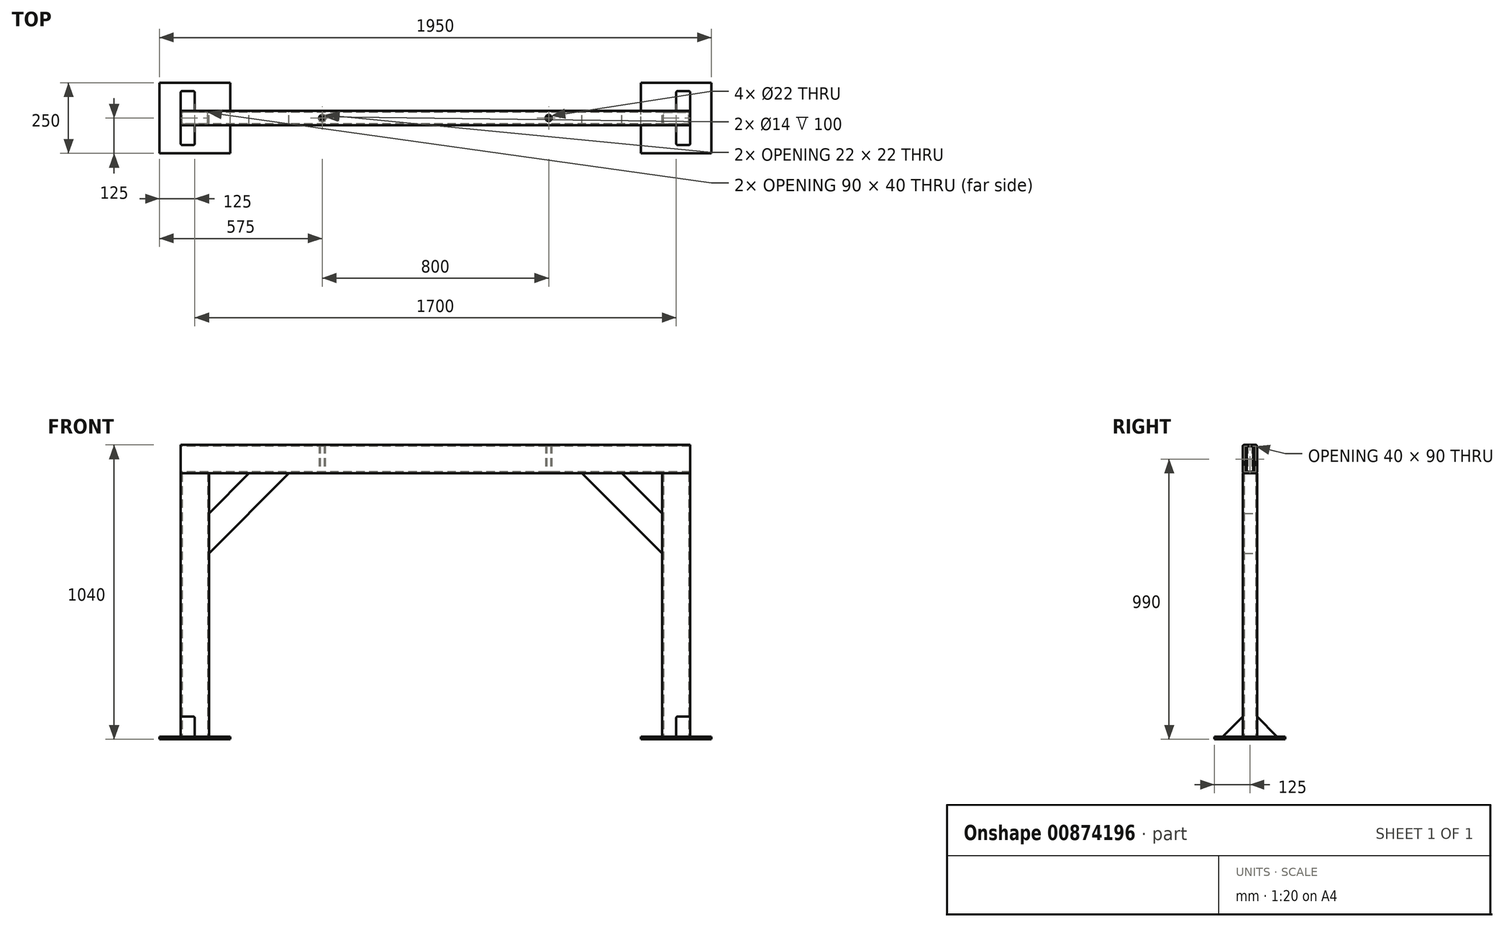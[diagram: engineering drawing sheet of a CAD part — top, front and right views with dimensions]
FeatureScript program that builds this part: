
annotation { "Feature Type Name" : "Feature", "Feature Type Description" : "" }
export const myFeature = defineFeature(function(context is Context, id is Id, definition is map)
    precondition{}
    {
        {
            var Q0;
            Q0=qCreatedBy(makeId("Top.planeOp"),FACE);
            var sketch = newSketch(context, id + "F0", { "sketchPlane" : qUnion([Q0])});
            skLineSegment(sketch, "E0.bottom", {"start": v(-804, -25) * mm, "end": v(-896, -25) * mm});
            skLineSegment(sketch, "E0.top", {"start": v(-804, 25) * mm, "end": v(-896, 25) * mm});
            skLineSegment(sketch, "E0.left", {"start": v(-800, -21) * mm, "end": v(-800, 21) * mm});
            skLineSegment(sketch, "E0.right", {"start": v(-900, -21) * mm, "end": v(-900, 21) * mm});
            skPoint(sketch, "E0.middle", {"position": v(-850, 0) * mm});
            skLineSegment(sketch, "E1.bottom", {"start": v(-808, -20) * mm, "end": v(-892, -20) * mm});
            skLineSegment(sketch, "E1.top", {"start": v(-808, 20) * mm, "end": v(-892, 20) * mm});
            skLineSegment(sketch, "E1.left", {"start": v(-805, -17) * mm, "end": v(-805, 17) * mm});
            skLineSegment(sketch, "E1.right", {"start": v(-895, -17) * mm, "end": v(-895, 17) * mm});
            skPoint(sketch, "E2.visualSharp", {"position": v(-895, 20) * mm});
            skArc(sketch, "E2.filletArc", {"start": v(-892, 20) * mm, "mid": v(-894.12, 19.12) * mm, "end": v(-895, 17) * mm});
            skPoint(sketch, "E3.visualSharp", {"position": v(-805, 20) * mm});
            skArc(sketch, "E3.filletArc", {"start": v(-805, 17) * mm, "mid": v(-805.88, 19.12) * mm, "end": v(-808, 20) * mm});
            skPoint(sketch, "E4.visualSharp", {"position": v(-805, -20) * mm});
            skArc(sketch, "E4.filletArc", {"start": v(-808, -20) * mm, "mid": v(-805.88, -19.12) * mm, "end": v(-805, -17) * mm});
            skPoint(sketch, "E5.visualSharp", {"position": v(-895, -20) * mm});
            skArc(sketch, "E5.filletArc", {"start": v(-895, -17) * mm, "mid": v(-894.12, -19.12) * mm, "end": v(-892, -20) * mm});
            skPoint(sketch, "E6.visualSharp", {"position": v(-900, 25) * mm});
            skArc(sketch, "E6.filletArc", {"start": v(-896, 25) * mm, "mid": v(-898.83, 23.83) * mm, "end": v(-900, 21) * mm});
            skPoint(sketch, "E7.visualSharp", {"position": v(-800, 25) * mm});
            skArc(sketch, "E7.filletArc", {"start": v(-800, 21) * mm, "mid": v(-801.17, 23.83) * mm, "end": v(-804, 25) * mm});
            skPoint(sketch, "E8.visualSharp", {"position": v(-800, -25) * mm});
            skArc(sketch, "E8.filletArc", {"start": v(-804, -25) * mm, "mid": v(-801.17, -23.83) * mm, "end": v(-800, -21) * mm});
            skPoint(sketch, "E9.visualSharp", {"position": v(-900, -25) * mm});
            skArc(sketch, "E9.filletArc", {"start": v(-900, -21) * mm, "mid": v(-898.83, -23.83) * mm, "end": v(-896, -25) * mm});
            skArc(sketch, "E10.MirrorCS", {"start": v(808, -20) * mm, "mid": v(805.88, -19.12) * mm, "end": v(805, -17) * mm});
            skArc(sketch, "E11.MirrorCS", {"start": v(800, 21) * mm, "mid": v(801.17, 23.83) * mm, "end": v(804, 25) * mm});
            skArc(sketch, "E12.MirrorCS", {"start": v(804, -25) * mm, "mid": v(801.17, -23.83) * mm, "end": v(800, -21) * mm});
            skArc(sketch, "E13.MirrorCS", {"start": v(892, 20) * mm, "mid": v(894.12, 19.12) * mm, "end": v(895, 17) * mm});
            skArc(sketch, "E14.MirrorCS", {"start": v(896, 25) * mm, "mid": v(898.83, 23.83) * mm, "end": v(900, 21) * mm});
            skArc(sketch, "E15.MirrorCS", {"start": v(805, 17) * mm, "mid": v(805.88, 19.12) * mm, "end": v(808, 20) * mm});
            skArc(sketch, "E16.MirrorCS", {"start": v(895, -17) * mm, "mid": v(894.12, -19.12) * mm, "end": v(892, -20) * mm});
            skArc(sketch, "E17.MirrorCS", {"start": v(900, -21) * mm, "mid": v(898.83, -23.83) * mm, "end": v(896, -25) * mm});
            skLineSegment(sketch, "E18.MirrorCS", {"start": v(900, -21) * mm, "end": v(900, 21) * mm});
            skPoint(sketch, "E19.MirrorP", {"position": v(850, 0) * mm});
            skLineSegment(sketch, "E20.MirrorCS", {"start": v(804, -25) * mm, "end": v(896, -25) * mm});
            skPoint(sketch, "E21.MirrorP", {"position": v(805, 20) * mm});
            skLineSegment(sketch, "E22.MirrorCS", {"start": v(805, -17) * mm, "end": v(805, 17) * mm});
            skLineSegment(sketch, "E23.MirrorCS", {"start": v(895, -17) * mm, "end": v(895, 17) * mm});
            skLineSegment(sketch, "E24.MirrorCS", {"start": v(800, -21) * mm, "end": v(800, 21) * mm});
            skLineSegment(sketch, "E25.MirrorCS", {"start": v(808, -20) * mm, "end": v(892, -20) * mm});
            skPoint(sketch, "E26.MirrorP", {"position": v(895, 20) * mm});
            skPoint(sketch, "E27.MirrorP", {"position": v(900, 25) * mm});
            skPoint(sketch, "E28.MirrorP", {"position": v(800, 25) * mm});
            skPoint(sketch, "E29.MirrorP", {"position": v(900, -25) * mm});
            skPoint(sketch, "E30.MirrorP", {"position": v(805, -20) * mm});
            skLineSegment(sketch, "E31.MirrorCS", {"start": v(808, 20) * mm, "end": v(892, 20) * mm});
            skLineSegment(sketch, "E32.MirrorCS", {"start": v(804, 25) * mm, "end": v(896, 25) * mm});
            skPoint(sketch, "E33.MirrorP", {"position": v(895, -20) * mm});
            skPoint(sketch, "E34.MirrorP", {"position": v(800, -25) * mm});
            skSolve(sketch);
        }
        {
            var Q0;
            Q0 = qSketchRegion(id + "F0", true);
            extrude(context, id + "F1", {"entities" : qUnion([Q0]), "depth" : 930 * mm, "offsetDistance" : 25 * mm});
        }
        {
            var Q0;
            Q0=makeQuery(id+"F1.opExtrude","SWEPT_FACE",FACE,{"disambiguationData":[OSD([sQuery(id+"F0.wireOp",EDGE,"E0.right")])]});
            var sketch = newSketch(context, id + "F2", { "sketchPlane" : qUnion([Q0])});
            skLineSegment(sketch, "E35.bottom", {"start": v(21, 930) * mm, "end": v(-21, 930) * mm});
            skLineSegment(sketch, "E35.top", {"start": v(21, 1030) * mm, "end": v(-21, 1030) * mm});
            skLineSegment(sketch, "E35.left", {"start": v(25, 934) * mm, "end": v(25, 1026) * mm});
            skLineSegment(sketch, "E35.right", {"start": v(-25, 934) * mm, "end": v(-25, 1026) * mm});
            skPoint(sketch, "E35.middle", {"position": v(0, 980) * mm});
            skPoint(sketch, "E35.middle.positionSnap0", {"position": v(0, 930) * mm});
            skPoint(sketch, "E35.centerSnap0", {"position": v(0, 930) * mm});
            skLineSegment(sketch, "E36.bottom", {"start": v(17, 935) * mm, "end": v(-17, 935) * mm});
            skLineSegment(sketch, "E36.top", {"start": v(17, 1025) * mm, "end": v(-17, 1025) * mm});
            skLineSegment(sketch, "E36.left", {"start": v(20, 938) * mm, "end": v(20, 1022) * mm});
            skLineSegment(sketch, "E36.right", {"start": v(-20, 938) * mm, "end": v(-20, 1022) * mm});
            skPoint(sketch, "E37.visualSharp", {"position": v(-20, 1025) * mm});
            skArc(sketch, "E37.filletArc", {"start": v(-17, 1025) * mm, "mid": v(-19.12, 1024.12) * mm, "end": v(-20, 1022) * mm});
            skPoint(sketch, "E38.visualSharp", {"position": v(20, 1025) * mm});
            skArc(sketch, "E38.filletArc", {"start": v(20, 1022) * mm, "mid": v(19.12, 1024.12) * mm, "end": v(17, 1025) * mm});
            skPoint(sketch, "E39.visualSharp", {"position": v(20, 935) * mm});
            skArc(sketch, "E39.filletArc", {"start": v(17, 935) * mm, "mid": v(19.12, 935.88) * mm, "end": v(20, 938) * mm});
            skPoint(sketch, "E40.visualSharp", {"position": v(-20, 935) * mm});
            skArc(sketch, "E40.filletArc", {"start": v(-20, 938) * mm, "mid": v(-19.12, 935.88) * mm, "end": v(-17, 935) * mm});
            skPoint(sketch, "E41.visualSharp", {"position": v(-25, 1030) * mm});
            skArc(sketch, "E41.filletArc", {"start": v(-21, 1030) * mm, "mid": v(-23.83, 1028.83) * mm, "end": v(-25, 1026) * mm});
            skPoint(sketch, "E42.visualSharp", {"position": v(25, 1030) * mm});
            skArc(sketch, "E42.filletArc", {"start": v(25, 1026) * mm, "mid": v(23.83, 1028.83) * mm, "end": v(21, 1030) * mm});
            skPoint(sketch, "E43.visualSharp", {"position": v(25, 930) * mm});
            skArc(sketch, "E43.filletArc", {"start": v(21, 930) * mm, "mid": v(23.83, 931.17) * mm, "end": v(25, 934) * mm});
            skPoint(sketch, "E44.visualSharp", {"position": v(-25, 930) * mm});
            skArc(sketch, "E44.filletArc", {"start": v(-25, 934) * mm, "mid": v(-23.83, 931.17) * mm, "end": v(-21, 930) * mm});
            skSolve(sketch);
        }
        {
            var Q0;
            Q0=makeQuery(id+"F2.imprint","IMPRINT",FACE,{"disambiguationData":[TD([[makeQuery(id+"F2.imprint","IMPRINT",EDGE,{"derivedFrom":sQuery(id+"F2.wireOp",EDGE,"E35.bottom")}),-1.0]])]});
            extrude(context, id + "F3", {"entities" : qUnion([Q0]), "oppositeDirection" : true, "depth" : 1800 * mm, "offsetDistance" : 25 * mm});
        }
        {
            var Q0;
            Q0=qCreatedBy(makeId("Front.planeOp"),FACE);
            var sketch = newSketch(context, id + "F4", { "sketchPlane" : qUnion([Q0])});
            skLineSegment(sketch, "E45.0", {"start": v(800, 788.58) * mm, "end": v(800, 647.16) * mm});
            skLineSegment(sketch, "E46.0", {"start": v(658.58, 930) * mm, "end": v(517.16, 930) * mm});
            skLineSegment(sketch, "E47", {"start": v(800, 647.16) * mm, "end": v(517.16, 930) * mm});
            skLineSegment(sketch, "E48.0", {"start": v(800, 788.58) * mm, "end": v(658.58, 930) * mm});
            skPoint(sketch, "E49.orphan", {"position": v(900, 930) * mm});
            skPoint(sketch, "E50.orphan", {"position": v(-900, 930) * mm});
            skPoint(sketch, "E51.orphan", {"position": v(800, 0) * mm});
            skLineSegment(sketch, "E52.MirrorCS", {"start": v(-800, 788.58) * mm, "end": v(-658.58, 930) * mm});
            skLineSegment(sketch, "E53.MirrorCS", {"start": v(-800, 647.16) * mm, "end": v(-517.16, 930) * mm});
            skLineSegment(sketch, "E54.MirrorCS", {"start": v(-800, 788.58) * mm, "end": v(-800, 647.16) * mm});
            skLineSegment(sketch, "E55.MirrorCS", {"start": v(-658.58, 930) * mm, "end": v(-517.16, 930) * mm});
            skPoint(sketch, "E56.orphan", {"position": v(800, 930) * mm});
            skPoint(sketch, "E57.orphan", {"position": v(-800, 930) * mm});
            skSolve(sketch);
        }
        {
            var Q0;
            Q0 = qSketchRegion(id + "F4", true);
            extrude(context, id + "F5", {"entities" : qUnion([Q0]), "endBound" : BoundingType.SYMMETRIC, "depth" : 50 * mm, "offsetDistance" : 25 * mm});
        }
        {
            var Q0;
            Q0=makeQuery(id+"F5.opExtrude","CAP_EDGE",EDGE,{"disambiguationData":[OSD([sQuery(id+"F4.wireOp",EDGE,"E47")])],"isStart":true});
            var Q1;
            Q1=makeQuery(id+"F5.opExtrude","CAP_EDGE",EDGE,{"disambiguationData":[OSD([sQuery(id+"F4.wireOp",EDGE,"E47")])],"isStart":false});
            var Q2;
            Q2=makeQuery(id+"F5.opExtrude","CAP_EDGE",EDGE,{"disambiguationData":[OSD([sQuery(id+"F4.wireOp",EDGE,"E53.MirrorCS")])],"isStart":true});
            var Q3;
            Q3=makeQuery(id+"F5.opExtrude","CAP_EDGE",EDGE,{"disambiguationData":[OSD([sQuery(id+"F4.wireOp",EDGE,"E53.MirrorCS")])],"isStart":false});
            fillet(context, id + "F6", {"entities" : qUnion([Q0, Q1, Q2, Q3]), "radius" : 5 * mm, "tangentPropagation" : true, "allowEdgeOverflow" : false});
        }
        {
            var Q0;
            Q0=makeQuery(id+"F1.opExtrude","CAP_FACE",FACE,{"disambiguationData":[OSD([sQuery(id+"F0.wireOp",EDGE,"E10.MirrorCS"),sQuery(id+"F0.wireOp",EDGE,"E11.MirrorCS"),sQuery(id+"F0.wireOp",EDGE,"E12.MirrorCS"),sQuery(id+"F0.wireOp",EDGE,"E13.MirrorCS"),sQuery(id+"F0.wireOp",EDGE,"E14.MirrorCS"),sQuery(id+"F0.wireOp",EDGE,"E15.MirrorCS"),sQuery(id+"F0.wireOp",EDGE,"E16.MirrorCS"),sQuery(id+"F0.wireOp",EDGE,"E17.MirrorCS"),sQuery(id+"F0.wireOp",EDGE,"E18.MirrorCS"),sQuery(id+"F0.wireOp",EDGE,"E20.MirrorCS"),sQuery(id+"F0.wireOp",EDGE,"E22.MirrorCS"),sQuery(id+"F0.wireOp",EDGE,"E23.MirrorCS"),sQuery(id+"F0.wireOp",EDGE,"E24.MirrorCS"),sQuery(id+"F0.wireOp",EDGE,"E25.MirrorCS"),sQuery(id+"F0.wireOp",EDGE,"E31.MirrorCS"),sQuery(id+"F0.wireOp",EDGE,"E32.MirrorCS")])],"isStart":true});
            var sketch = newSketch(context, id + "F7", { "sketchPlane" : qUnion([Q0])});
            skLineSegment(sketch, "E58.bottom", {"start": v(725, 125) * mm, "end": v(975, 125) * mm});
            skLineSegment(sketch, "E58.top", {"start": v(725, -125) * mm, "end": v(975, -125) * mm});
            skLineSegment(sketch, "E58.left", {"start": v(725, 125) * mm, "end": v(725, -125) * mm});
            skLineSegment(sketch, "E58.right", {"start": v(975, 125) * mm, "end": v(975, -125) * mm});
            skPoint(sketch, "E58.middle", {"position": v(850, 0) * mm});
            skLineSegment(sketch, "E59.MirrorCS", {"start": v(-725, 125) * mm, "end": v(-975, 125) * mm});
            skLineSegment(sketch, "E60.MirrorCS", {"start": v(-725, -125) * mm, "end": v(-975, -125) * mm});
            skLineSegment(sketch, "E61.MirrorCS", {"start": v(-975, 125) * mm, "end": v(-975, -125) * mm});
            skPoint(sketch, "E62.MirrorP", {"position": v(-850, 0) * mm});
            skLineSegment(sketch, "E63.MirrorCS", {"start": v(-725, 125) * mm, "end": v(-725, -125) * mm});
            skSolve(sketch);
        }
        {
            var Q0;
            Q0 = qSketchRegion(id + "F7", true);
            extrude(context, id + "F8", {"entities" : qUnion([Q0]), "depth" : 10 * mm, "offsetDistance" : 25 * mm});
        }
        {
            var Q0;
            Q0=makeQuery(id+"F1.opExtrude","SWEPT_FACE",FACE,{"disambiguationData":[OSD([sQuery(id+"F0.wireOp",EDGE,"E18.MirrorCS")])]});
            var sketch = newSketch(context, id + "F9", { "sketchPlane" : qUnion([Q0])});
            skLineSegment(sketch, "E64.0", {"start": v(25, 70.71) * mm, "end": v(25, 0) * mm});
            skLineSegment(sketch, "E65.0", {"start": v(25, 0) * mm, "end": v(95.71, 0) * mm});
            skLineSegment(sketch, "E66", {"start": v(25, 70.71) * mm, "end": v(95.71, 0) * mm});
            skPoint(sketch, "E67.orphan", {"position": v(25, 930) * mm});
            skPoint(sketch, "E68.orphan", {"position": v(125, 0) * mm});
            skPoint(sketch, "E69.orphan", {"position": v(-125, 0) * mm});
            skLineSegment(sketch, "E70.MirrorCS", {"start": v(-25, 70.71) * mm, "end": v(-95.71, 0) * mm});
            skLineSegment(sketch, "E71.MirrorCS", {"start": v(-25, 0) * mm, "end": v(-95.71, 0) * mm});
            skLineSegment(sketch, "E72.MirrorCS", {"start": v(-25, 70.71) * mm, "end": v(-25, 0) * mm});
            skSolve(sketch);
        }
        {
            var Q0;
            Q0=makeQuery(id+"F9.imprint","IMPRINT",FACE,{"disambiguationData":[TD([[makeQuery(id+"F9.imprint","IMPRINT",EDGE,{"derivedFrom":sQuery(id+"F9.wireOp",EDGE,"E70.MirrorCS")}),1.0]])]});
            var Q1;
            Q1=makeQuery(id+"F9.imprint","IMPRINT",FACE,{"disambiguationData":[TD([[makeQuery(id+"F9.imprint","IMPRINT",EDGE,{"derivedFrom":sQuery(id+"F9.wireOp",EDGE,"E64.0")}),1.0]])]});
            extrude(context, id + "F10", {"entities" : qUnion([Q0, Q1]), "oppositeDirection" : true, "depth" : 50 * mm, "offsetDistance" : 25 * mm});
        }
        {
            var Q0;
            Q0=makeQuery(id+"F10.opExtrude","CAP_EDGE",EDGE,{"disambiguationData":[OSD([sQuery(id+"F9.wireOp",EDGE,"E66")])],"isStart":true});
            var Q1;
            Q1=makeQuery(id+"F10.opExtrude","CAP_EDGE",EDGE,{"disambiguationData":[OSD([sQuery(id+"F9.wireOp",EDGE,"E66")])],"isStart":false});
            var Q2;
            Q2=makeQuery(id+"F10.opExtrude","CAP_EDGE",EDGE,{"disambiguationData":[OSD([sQuery(id+"F9.wireOp",EDGE,"E70.MirrorCS")])],"isStart":true});
            var Q3;
            Q3=makeQuery(id+"F10.opExtrude","CAP_EDGE",EDGE,{"disambiguationData":[OSD([sQuery(id+"F9.wireOp",EDGE,"E70.MirrorCS")])],"isStart":false});
            fillet(context, id + "F11", {"entities" : qUnion([Q0, Q1, Q2, Q3]), "radius" : 5 * mm, "tangentPropagation" : true, "allowEdgeOverflow" : false});
        }
        {
            var Q0;
            Q0=makeQuery(id+"F10.opExtrude","SWEPT_BODY",BODY,{"disambiguationData":[OSD([sQuery(id+"F9.wireOp",EDGE,"E70.MirrorCS"),sQuery(id+"F9.wireOp",EDGE,"E71.MirrorCS"),sQuery(id+"F9.wireOp",EDGE,"E72.MirrorCS")])]});
            var Q1;
            Q1=makeQuery(id+"F10.opExtrude","SWEPT_BODY",BODY,{"disambiguationData":[OSD([sQuery(id+"F9.wireOp",EDGE,"E64.0"),sQuery(id+"F9.wireOp",EDGE,"E65.0"),sQuery(id+"F9.wireOp",EDGE,"E66")])]});
            var Q2;
            Q2=qCreatedBy(makeId("Right.planeOp"),FACE);
            mirror(context, id + "F12", {"entities" : qUnion([Q0, Q1]), "mirrorPlane" : qUnion([Q2])});
        }
        {
            var Q0;
            Q0=makeQuery(id+"F3.opExtrude","SWEPT_FACE",FACE,{"disambiguationData":[OSD([sQuery(id+"F2.wireOp",EDGE,"E35.bottom")])]});
            var sketch = newSketch(context, id + "F13", { "sketchPlane" : qUnion([Q0])});
            skCircle(sketch, "E73", {"center": v(-400, 0) * mm, "radius": 11 * mm});
            skCircle(sketch, "E74.MirrorC", {"center": v(400, 0) * mm, "radius": 11 * mm});
            skSolve(sketch);
        }
        {
            var Q0;
            Q0 = qSketchRegion(id + "F13", true);
            extrude(context, id + "F14", {"entities" : qUnion([Q0]), "operationType" : NewBodyOperationType.REMOVE, "oppositeDirection" : true, "depth" : 100 * mm, "offsetDistance" : 25 * mm});
        }
        {
            var Q0;
            Q0=makeQuery(id+"F3.opExtrude","SWEPT_FACE",FACE,{"disambiguationData":[OSD([sQuery(id+"F2.wireOp",EDGE,"E35.bottom")])]});
            var sketch = newSketch(context, id + "F15", { "sketchPlane" : qUnion([Q0])});
            skCircle(sketch, "E75", {"center": v(-400, 0) * mm, "radius": 11 * mm});
            skCircle(sketch, "E76", {"center": v(-400, 0) * mm, "radius": 7 * mm});
            skCircle(sketch, "E77.MirrorC", {"center": v(400, 0) * mm, "radius": 11 * mm});
            skCircle(sketch, "E78.MirrorC", {"center": v(400, 0) * mm, "radius": 7 * mm});
            skSolve(sketch);
        }
        {
            var Q0;
            Q0 = qSketchRegion(id + "F15", true);
            extrude(context, id + "F16", {"entities" : qUnion([Q0]), "oppositeDirection" : true, "depth" : 100 * mm, "offsetDistance" : 25 * mm});
        }
        {
            var Q0;
            Q0=makeQuery(id+"F5.opExtrude","CAP_EDGE",EDGE,{"disambiguationData":[OSD([sQuery(id+"F4.wireOp",EDGE,"E52.MirrorCS")])],"isStart":false});
            var Q1;
            Q1=makeQuery(id+"F5.opExtrude","CAP_EDGE",EDGE,{"disambiguationData":[OSD([sQuery(id+"F4.wireOp",EDGE,"E52.MirrorCS")])],"isStart":true});
            fillet(context, id + "F17", {"entities" : qUnion([Q0, Q1]), "radius" : 5 * mm, "tangentPropagation" : true, "allowEdgeOverflow" : false});
        }
        {
            var Q0;
            Q0=makeQuery(id+"F5.opExtrude","CAP_EDGE",EDGE,{"disambiguationData":[OSD([sQuery(id+"F4.wireOp",EDGE,"E48.0")])],"isStart":true});
            var Q1;
            Q1=makeQuery(id+"F5.opExtrude","CAP_EDGE",EDGE,{"disambiguationData":[OSD([sQuery(id+"F4.wireOp",EDGE,"E48.0")])],"isStart":false});
            fillet(context, id + "F18", {"entities" : qUnion([Q0, Q1]), "radius" : 5 * mm, "tangentPropagation" : true, "allowEdgeOverflow" : false});
        }
    });
